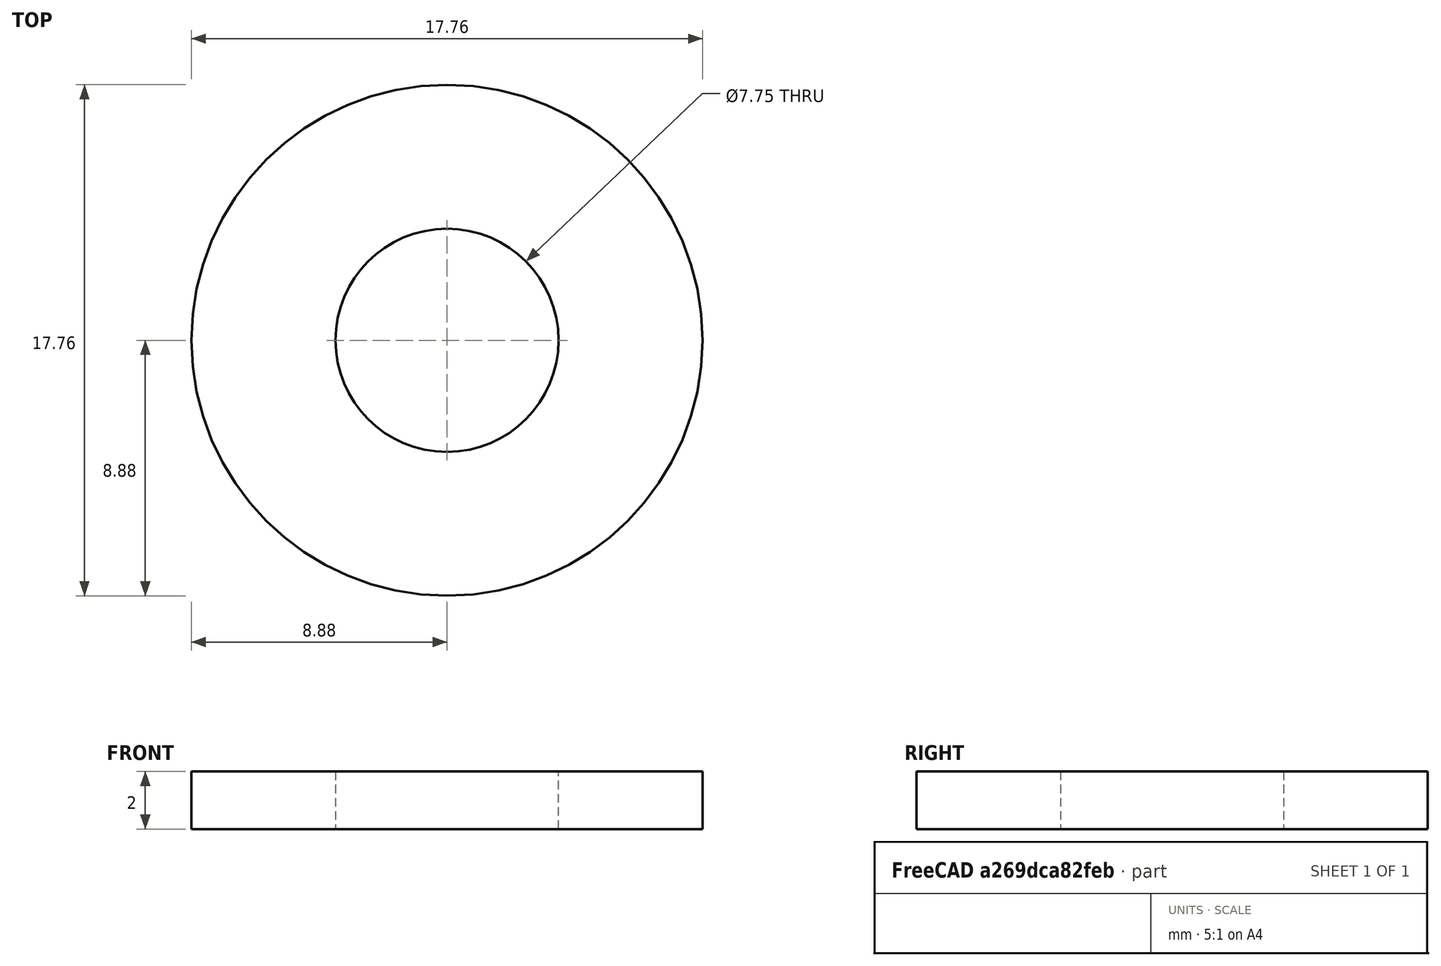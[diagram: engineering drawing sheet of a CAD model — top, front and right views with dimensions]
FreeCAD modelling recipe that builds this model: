
FCSTD DOCUMENT  (FreeCAD 0.19R24276 (Git))
Label: Test_DC_Mount
License: All rights reserved
LicenseURL: http://en.wikipedia.org/wiki/All_rights_reserved
objects: Sketcher::SketchObject×1, PartDesign::Pad×1, PartDesign::Body×1
note: 4 computed .brp shape members not serialized (recipe doc carries the construction recipe); baked Part::Feature solids carry a one-line shape summary decoded from their .brp

FEATURE [Sketcher::SketchObject] Sketch
  FullyConstrained = true
  MapMode = 5
  Support = -> [XY_Plane]
  sketch-geometry (4):
    g0: Circle CenterX=0 CenterY=0 CenterZ=0 NormalX=0 NormalY=0 NormalZ=1 AngleXU=0 Radius=3.875
    g1: Circle CenterX=0 CenterY=0 CenterZ=0 NormalX=0 NormalY=0 NormalZ=1 AngleXU=0 Radius=8.875
    g2: GeomPoint X=0 Y=8.875 Z=0
    g3: GeomPoint X=0 Y=3.875 Z=0
  constraints (8):
    c: Coincident(g0,g-1)
    c: Coincident(g1,g0)
    c: PointOnObject(g2,g1)
    c: PointOnObject(g3,g0)
    c: PointOnObject(g3,g-2)
    c: PointOnObject(g2,g-2)
    c: Distance(g3,g2) = 5
    c: Diameter(g0) = 7.75
FEATURE [PartDesign::Pad] Pad
  Direction = (1,1,1)
  Length = 2
  Length2 = 100
  Profile = -> Sketch
  Type = 0
FEATURE [PartDesign::Body] Body
  Group = -> [Sketch,Pad]
  Origin = -> Origin
  Tip = -> Pad
